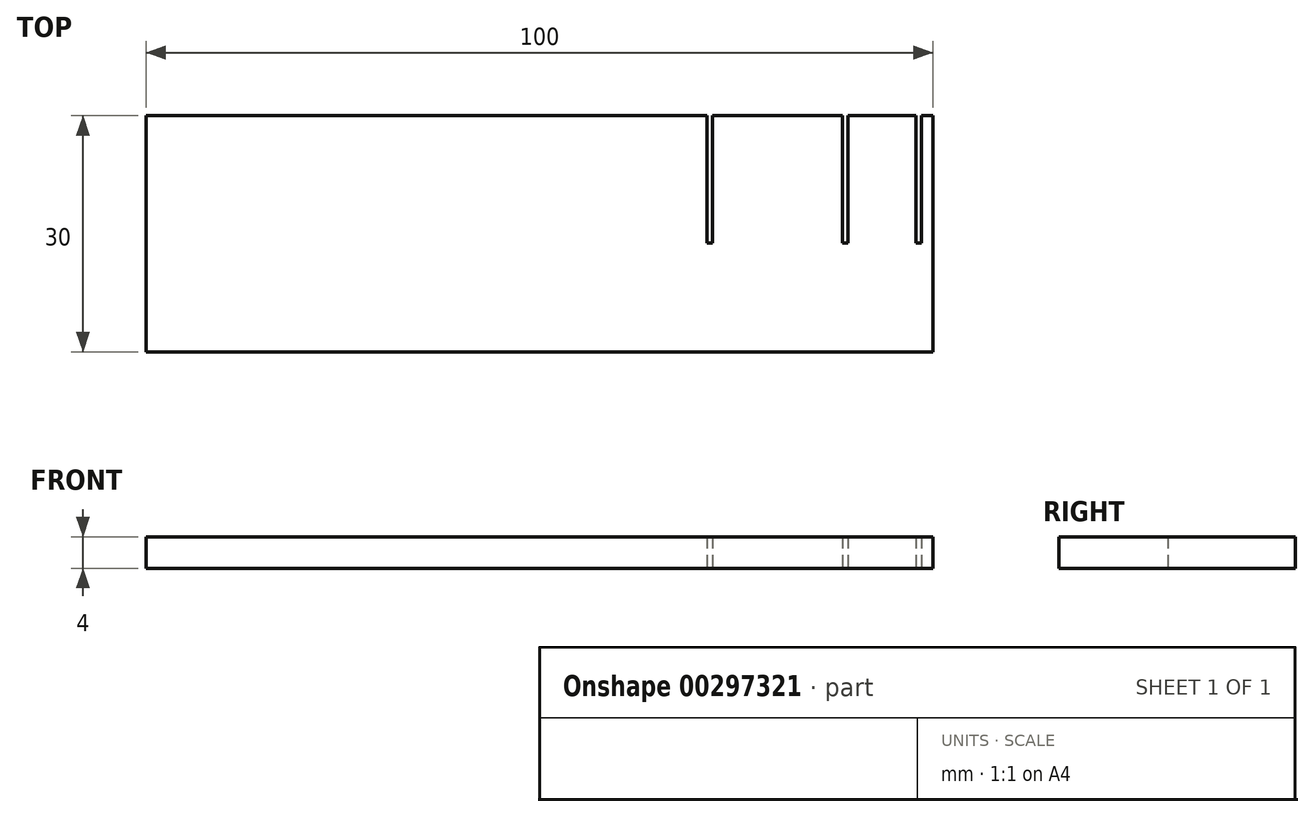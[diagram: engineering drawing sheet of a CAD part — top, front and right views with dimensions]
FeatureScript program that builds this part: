
annotation { "Feature Type Name" : "Feature", "Feature Type Description" : "" }
export const myFeature = defineFeature(function(context is Context, id is Id, definition is map)
    precondition{}
    {
        {
            var Q0;
            Q0=qCreatedBy(makeId("Top.planeOp"),FACE);
            var sketch = newSketch(context, id + "F0", { "sketchPlane" : qUnion([Q0])});
            skLineSegment(sketch, "E0.bottom", {"start": v(50, -15) * mm, "end": v(-50, -15) * mm});
            skLineSegment(sketch, "E0.top", {"start": v(50, 15) * mm, "end": v(-50, 15) * mm});
            skLineSegment(sketch, "E0.left", {"start": v(50, -15) * mm, "end": v(50, 15) * mm});
            skLineSegment(sketch, "E0.right", {"start": v(-50, -15) * mm, "end": v(-50, 15) * mm});
            skPoint(sketch, "E0.middle", {"position": v(0, 0) * mm});
            skSolve(sketch);
        }
        {
            var Q0;
            Q0=qCreatedBy(makeId("Top.planeOp"),FACE);
            var sketch = newSketch(context, id + "F1", { "sketchPlane" : qUnion([Q0])});
            skPoint(sketch, "E1.middle", {"position": v(0, 0) * mm});
            skLineSegment(sketch, "E2.bottom", {"start": v(21.3, -1.2) * mm, "end": v(22, -1.2) * mm});
            skLineSegment(sketch, "E2.top", {"start": v(21.3, 27.79) * mm, "end": v(22, 27.79) * mm});
            skLineSegment(sketch, "E2.left", {"start": v(21.3, -1.2) * mm, "end": v(21.3, 27.79) * mm});
            skLineSegment(sketch, "E2.right", {"start": v(22, -1.2) * mm, "end": v(22, 27.79) * mm});
            skLineSegment(sketch, "E3.bottom", {"start": v(47.8, -1.2) * mm, "end": v(48.5, -1.2) * mm});
            skLineSegment(sketch, "E3.top", {"start": v(47.8, 38.42) * mm, "end": v(48.5, 38.42) * mm});
            skLineSegment(sketch, "E3.left", {"start": v(47.8, -1.2) * mm, "end": v(47.8, 38.42) * mm});
            skLineSegment(sketch, "E3.right", {"start": v(48.5, -1.2) * mm, "end": v(48.5, 38.42) * mm});
            skLineSegment(sketch, "E4.bottom", {"start": v(38.47, -1.2) * mm, "end": v(39.17, -1.2) * mm});
            skLineSegment(sketch, "E4.top", {"start": v(38.47, 25.3) * mm, "end": v(39.17, 25.3) * mm});
            skLineSegment(sketch, "E4.left", {"start": v(38.47, -1.2) * mm, "end": v(38.47, 25.3) * mm});
            skLineSegment(sketch, "E4.right", {"start": v(39.17, -1.2) * mm, "end": v(39.17, 25.3) * mm});
            skSolve(sketch);
        }
        {
            var Q0;
            Q0=qSketchRegion(id+"F0",true);
            extrude(context, id + "F2", {"entities" : qUnion([Q0]), "depth" : 4 * mm});
        }
        {
            var Q0;
            Q0=qSketchRegion(id+"F1",true);
            extrude(context, id + "F3", {"entities" : qUnion([Q0]), "operationType" : NewBodyOperationType.REMOVE, "depth" : 4 * mm});
        }
    });
